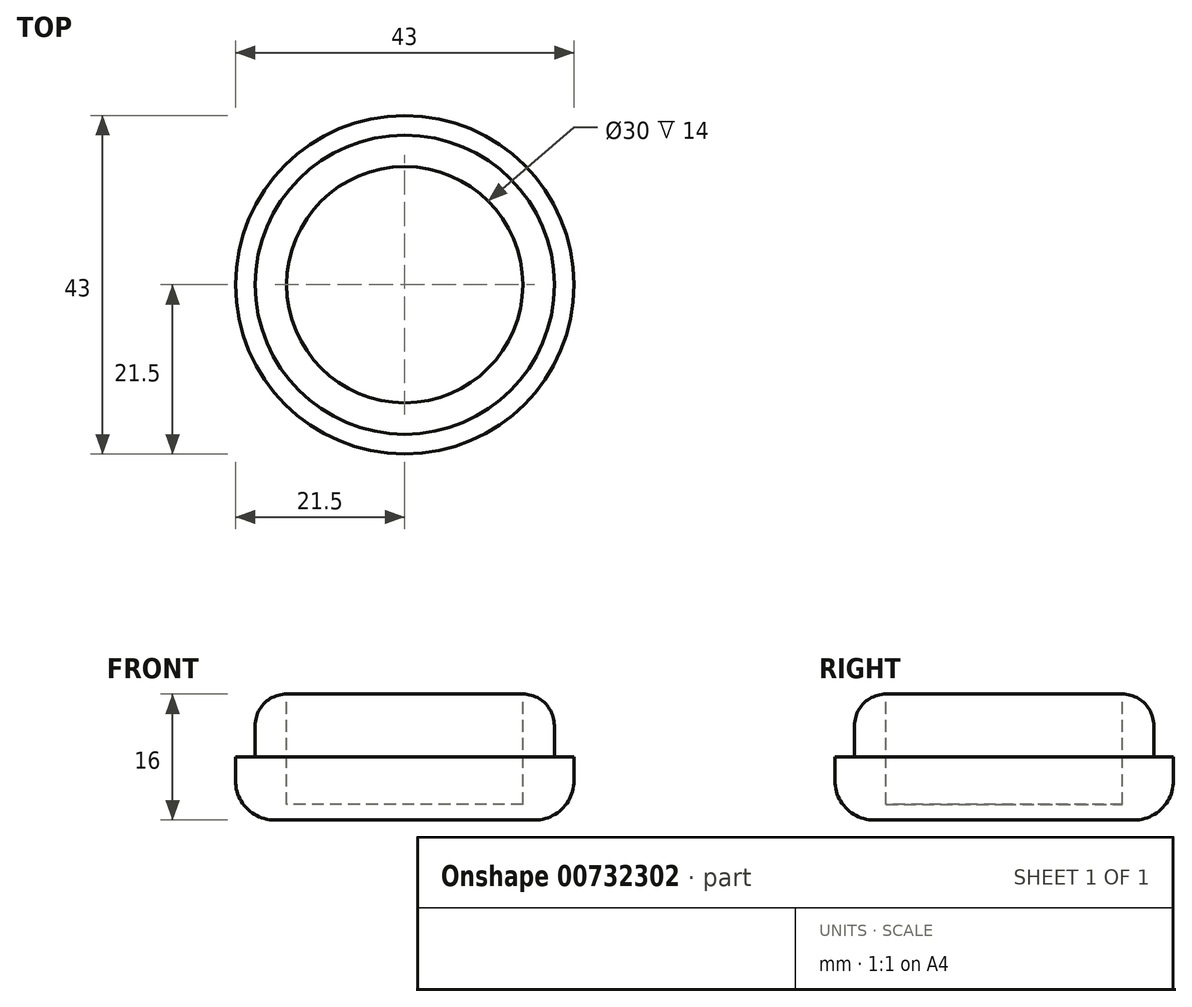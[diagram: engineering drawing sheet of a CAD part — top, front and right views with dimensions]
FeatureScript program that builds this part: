
annotation { "Feature Type Name" : "Feature", "Feature Type Description" : "" }
export const myFeature = defineFeature(function(context is Context, id is Id, definition is map)
    precondition{}
    {
        {
            var Q0;
            Q0=qCreatedBy(makeId("Top.planeOp"),FACE);
            var sketch = newSketch(context, id + "F0", { "sketchPlane" : qUnion([Q0])});
            skCircle(sketch, "E0", {"center": v(0, 0) * mm, "radius": 21.5 * mm});
            skSolve(sketch);
        }
        {
            var Q0;
            Q0 = qSketchRegion(id + "F0", true);
            extrude(context, id + "F1", {"entities" : qUnion([Q0]), "depth" : 8 * mm, "offsetDistance" : 25 * mm});
        }
        {
            var Q0;
            Q0=makeQuery(id+"F1.opExtrude","CAP_FACE",FACE,{"disambiguationData":[OSD([sQuery(id+"F0.wireOp",EDGE,"E0")])],"isStart":false});
            var sketch = newSketch(context, id + "F2", { "sketchPlane" : qUnion([Q0])});
            skCircle(sketch, "E1", {"center": v(0, 0) * mm, "radius": 19 * mm});
            skSolve(sketch);
        }
        {
            var Q0;
            Q0 = qSketchRegion(id + "F2", true);
            extrude(context, id + "F3", {"entities" : qUnion([Q0]), "operationType" : NewBodyOperationType.ADD, "depth" : 8 * mm, "offsetDistance" : 25 * mm});
        }
        {
            var Q0;
            Q0=makeQuery(id+"F3.opExtrude","CAP_EDGE",EDGE,{"disambiguationData":[OSD([sQuery(id+"F2.wireOp",EDGE,"E1")])],"isStart":false});
            fillet(context, id + "F4", {"entities" : qUnion([Q0]), "radius" : 4 * mm, "tangentPropagation" : true, "allowEdgeOverflow" : false});
        }
        {
            var Q0;
            Q0=makeQuery(id+"F1.opExtrude","CAP_FACE",FACE,{"disambiguationData":[OSD([sQuery(id+"F0.wireOp",EDGE,"E0")])],"isStart":true});
            fillet(context, id + "F5", {"entities" : qUnion([Q0]), "radius" : 5 * mm, "tangentPropagation" : true, "allowEdgeOverflow" : false});
        }
        {
            var Q0;
            Q0=makeQuery(id+"F3.opExtrude","CAP_FACE",FACE,{"disambiguationData":[OSD([sQuery(id+"F2.wireOp",EDGE,"E1")])],"isStart":false});
            var sketch = newSketch(context, id + "F6", { "sketchPlane" : qUnion([Q0])});
            skCircle(sketch, "E2", {"center": v(0, 0) * mm, "radius": 15 * mm});
            skSolve(sketch);
        }
        {
            var Q0;
            Q0 = qSketchRegion(id + "F6", true);
            extrude(context, id + "F7", {"entities" : qUnion([Q0]), "operationType" : NewBodyOperationType.REMOVE, "oppositeDirection" : true, "depth" : 14 * mm, "offsetDistance" : 25 * mm});
        }
    });
